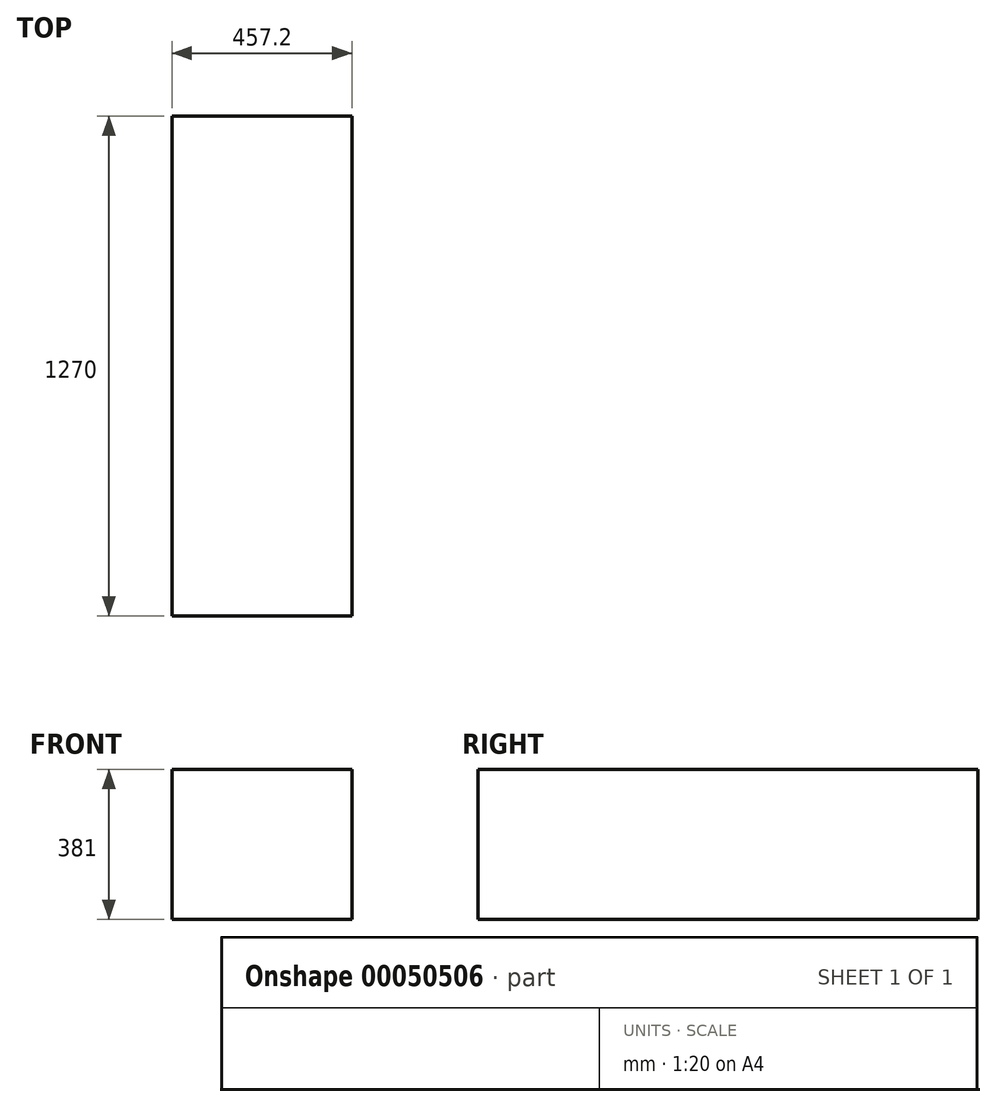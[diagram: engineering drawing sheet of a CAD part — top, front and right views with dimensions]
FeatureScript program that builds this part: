
annotation { "Feature Type Name" : "Feature", "Feature Type Description" : "" }
export const myFeature = defineFeature(function(context is Context, id is Id, definition is map)
    precondition{}
    {
        {
            var Q0;
            Q0=qCreatedBy(makeId("Right.planeOp"),FACE);
            var sketch = newSketch(context, id + "F0", { "sketchPlane" : qUnion([Q0])});
            skLineSegment(sketch, "E0.rect.bottom", {"start": v(635, 190.5) * mm, "end": v(-635, 190.5) * mm});
            skLineSegment(sketch, "E0.rect.top", {"start": v(635, -190.5) * mm, "end": v(-635, -190.5) * mm});
            skLineSegment(sketch, "E0.rect.left", {"start": v(635, 190.5) * mm, "end": v(635, -190.5) * mm});
            skLineSegment(sketch, "E0.rect.right", {"start": v(-635, 190.5) * mm, "end": v(-635, -190.5) * mm});
            skPoint(sketch, "E0.rect.middle", {"position": v(0, 0) * mm});
            skSolve(sketch);
        }
        {
            var Q0;
            Q0 = qSketchRegion(id + "F0", true);
            extrude(context, id + "F1", {"entities" : qUnion([Q0]), "endBound" : BoundingType.SYMMETRIC, "depth" : 457.2 * mm});
        }
    });
